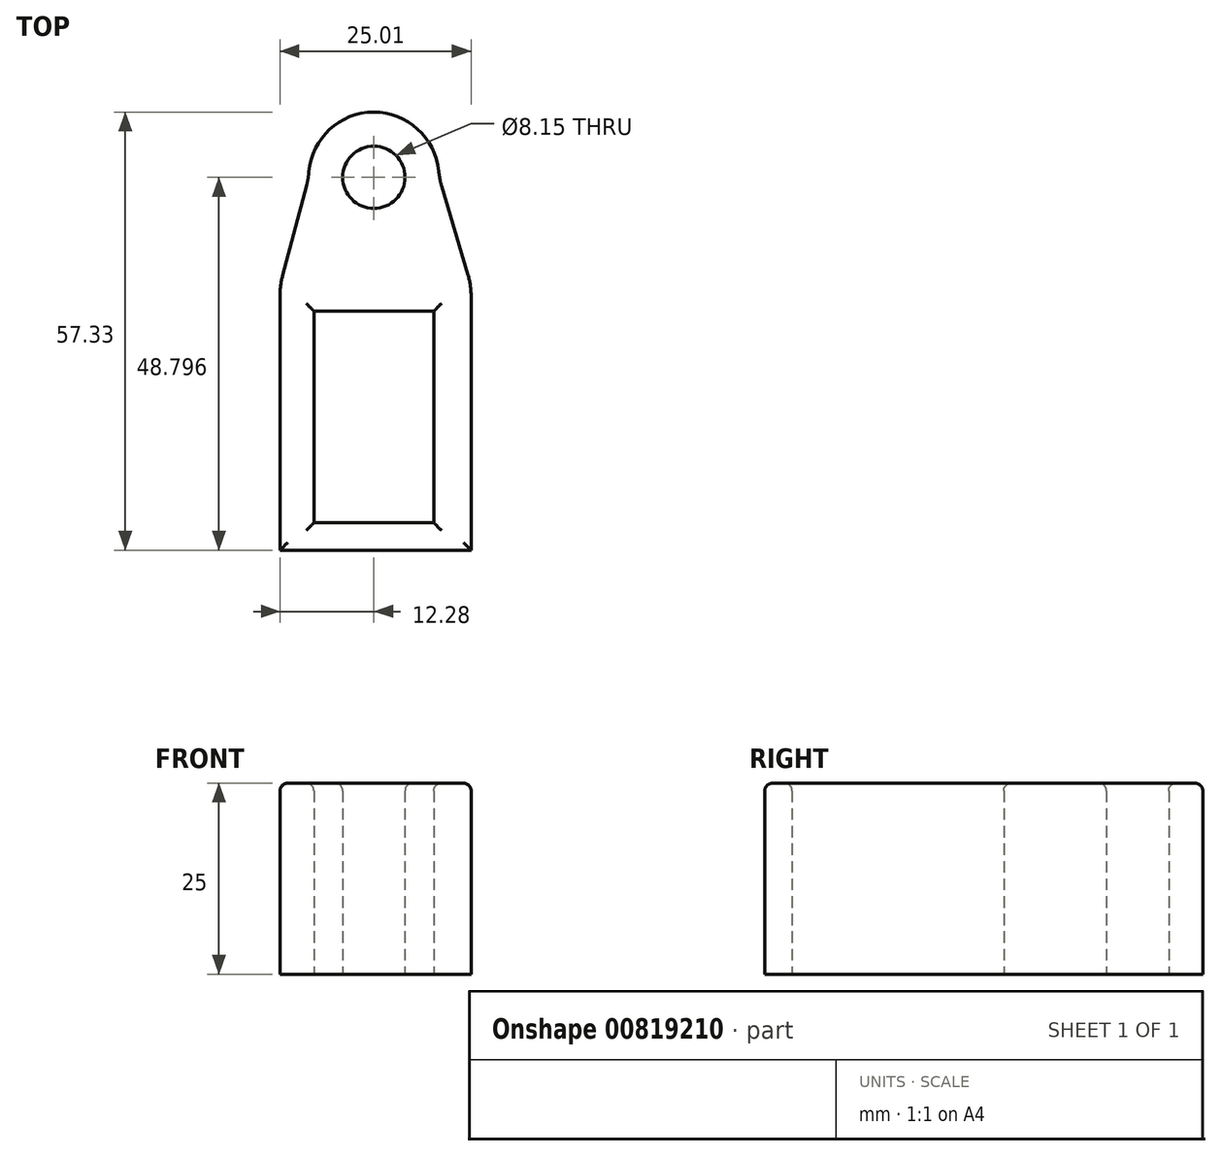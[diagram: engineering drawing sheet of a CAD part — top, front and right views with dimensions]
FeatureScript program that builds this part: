
annotation { "Feature Type Name" : "Feature", "Feature Type Description" : "" }
export const myFeature = defineFeature(function(context is Context, id is Id, definition is map)
    precondition{}
    {
        {
            var Q0;
            Q0=qCreatedBy(makeId("Top.planeOp"),FACE);
            var sketch = newSketch(context, id + "F0", { "sketchPlane" : qUnion([Q0])});
            skLineSegment(sketch, "E0.bottom", {"start": v(12.72, 17.25) * mm, "end": v(-12.28, 17.25) * mm});
            skPoint(sketch, "E0.middle", {"position": v(0, 0) * mm});
            skLineSegment(sketch, "E1.bottom", {"start": v(7.85, -13.85) * mm, "end": v(-7.85, -13.85) * mm});
            skLineSegment(sketch, "E1.top", {"start": v(7.85, 13.85) * mm, "end": v(-7.85, 13.85) * mm});
            skLineSegment(sketch, "E1.left", {"start": v(7.85, -13.85) * mm, "end": v(7.85, 13.85) * mm});
            skLineSegment(sketch, "E1.right", {"start": v(-7.85, -13.85) * mm, "end": v(-7.85, 13.85) * mm});
            skLineSegment(sketch, "E2", {"start": v(-12.27, -17.43) * mm, "end": v(12.72, -17.42) * mm});
            skLineSegment(sketch, "E3", {"start": v(-12.28, 17.25) * mm, "end": v(-12.27, -17.43) * mm});
            skLineSegment(sketch, "E4", {"start": v(12.72, 17.25) * mm, "end": v(12.72, -17.42) * mm});
            skCircle(sketch, "E5", {"center": v(0, 31.37) * mm, "radius": 4.08 * mm});
            skCircle(sketch, "E6", {"center": v(0, 31.37) * mm, "radius": 8.53 * mm});
            skLineSegment(sketch, "E7", {"start": v(-12.28, 17.25) * mm, "end": v(-8.53, 31.37) * mm});
            skLineSegment(sketch, "E8", {"start": v(12.73, 17.25) * mm, "end": v(8.53, 31.37) * mm});
            skSolve(sketch);
        }
        {
            var Q0;
            Q0=makeQuery(id+"F0.imprint","IMPRINT",FACE,{"disambiguationData":[TD([[makeQuery(id+"F0.imprint","IMPRINT",EDGE,{"derivedFrom":sQuery(id+"F0.wireOp",EDGE,"E0.bottom")}),1.0]])]});
            var Q1;
            Q1=makeQuery(id+"F0.imprint","IMPRINT",FACE,{"disambiguationData":[TD([[makeQuery(id+"F0.imprint","IMPRINT",EDGE,{"derivedFrom":sQuery(id+"F0.wireOp",EDGE,"E0.bottom")}),-1.0]])]});
            var Q2;
            Q2=makeQuery(id+"F0.imprint","IMPRINT",FACE,{"disambiguationData":[TD([[makeQuery(id+"F0.imprint","IMPRINT",EDGE,{"derivedFrom":sQuery(id+"F0.wireOp",EDGE,"E5")}),-1.0]])]});
            extrude(context, id + "F1", {"entities" : qUnion([Q0, Q1, Q2]), "depth" : 25 * mm, "offsetDistance" : 25 * mm});
        }
        {
            var Q0;
            Q0=makeQuery(id+"F1.opExtrude","SWEPT_EDGE",EDGE,{"disambiguationData":[OSD([sQuery(id+"F0.wireOp",EDGE,"E0.bottom"),sQuery(id+"F0.wireOp",EDGE,"E4"),sQuery(id+"F0.wireOp",EDGE,"E8")])]});
            var Q1;
            Q1=makeQuery(id+"F1.opExtrude","SWEPT_EDGE",EDGE,{"disambiguationData":[OSD([sQuery(id+"F0.wireOp",EDGE,"E6"),sQuery(id+"F0.wireOp",EDGE,"E8")])]});
            var Q2;
            Q2=makeQuery(id+"F1.opExtrude","SWEPT_EDGE",EDGE,{"disambiguationData":[OSD([sQuery(id+"F0.wireOp",EDGE,"E6"),sQuery(id+"F0.wireOp",EDGE,"E7")])]});
            var Q3;
            Q3=makeQuery(id+"F1.opExtrude","SWEPT_EDGE",EDGE,{"disambiguationData":[OSD([sQuery(id+"F0.wireOp",EDGE,"E0.bottom"),sQuery(id+"F0.wireOp",EDGE,"E3"),sQuery(id+"F0.wireOp",EDGE,"E7")])]});
            fillet(context, id + "F2", {"entities" : qUnion([Q0, Q1, Q2, Q3]), "radius" : 10 * mm, "tangentPropagation" : true, "allowEdgeOverflow" : false});
        }
        {
            var Q0;
            Q0=makeQuery(id+"F1.opExtrude","CAP_FACE",FACE,{"disambiguationData":[OSD([sQuery(id+"F0.wireOp",EDGE,"E1.bottom"),sQuery(id+"F0.wireOp",EDGE,"E1.top"),sQuery(id+"F0.wireOp",EDGE,"E1.left"),sQuery(id+"F0.wireOp",EDGE,"E1.right"),sQuery(id+"F0.wireOp",EDGE,"E2"),sQuery(id+"F0.wireOp",EDGE,"E3"),sQuery(id+"F0.wireOp",EDGE,"E4"),sQuery(id+"F0.wireOp",EDGE,"E5"),sQuery(id+"F0.wireOp",EDGE,"E6"),sQuery(id+"F0.wireOp",EDGE,"E7"),sQuery(id+"F0.wireOp",EDGE,"E8")])],"isStart":false});
            fillet(context, id + "F3", {"entities" : qUnion([Q0]), "radius" : 1 * mm, "tangentPropagation" : true, "allowEdgeOverflow" : false});
        }
    });
